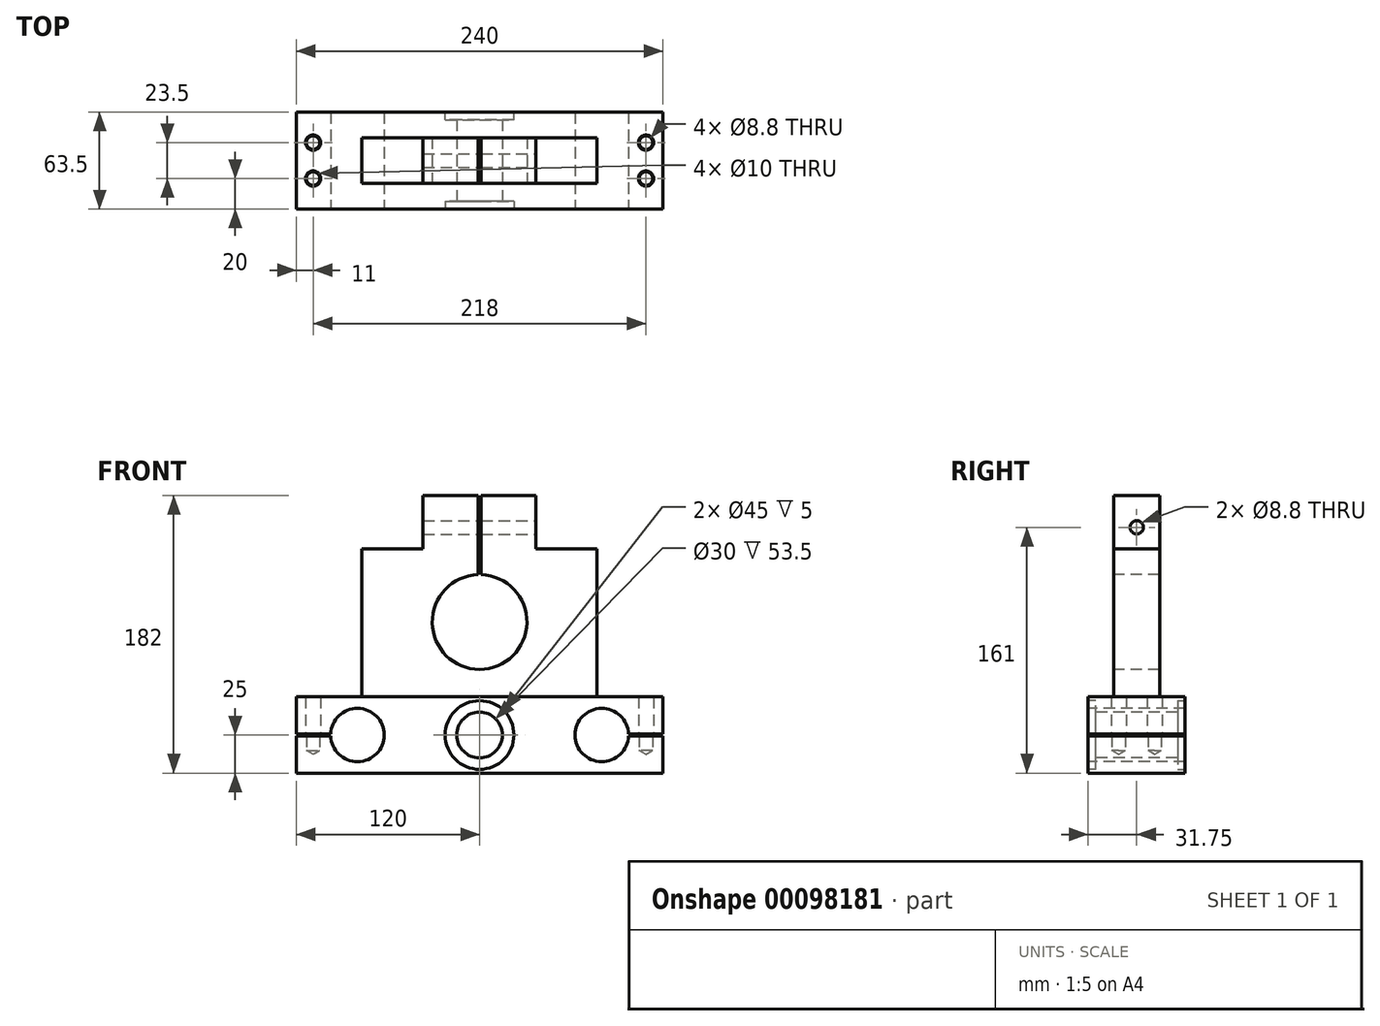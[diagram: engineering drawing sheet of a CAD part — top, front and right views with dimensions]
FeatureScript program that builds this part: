
annotation { "Feature Type Name" : "Feature", "Feature Type Description" : "" }
export const myFeature = defineFeature(function(context is Context, id is Id, definition is map)
    precondition{}
    {
        {
            var Q0;
            Q0=qCreatedBy(makeId("Front.planeOp"),FACE);
            var sketch = newSketch(context, id + "F0", { "sketchPlane" : qUnion([Q0])});
            skLineSegment(sketch, "E0.bottom", {"start": v(0, 0) * mm, "end": v(240, 0) * mm});
            skLineSegment(sketch, "E0.top", {"start": v(0, 50) * mm, "end": v(240, 50) * mm});
            skLineSegment(sketch, "E0.left", {"start": v(0, 0) * mm, "end": v(0, 50) * mm});
            skLineSegment(sketch, "E0.right", {"start": v(240, 0) * mm, "end": v(240, 50) * mm});
            skSolve(sketch);
        }
        {
            var Q0;
            Q0=makeQuery(id+"F0.imprint","IMPRINT",FACE,{"disambiguationData":[TD([[makeQuery(id+"F0.imprint","IMPRINT",EDGE,{"derivedFrom":sQuery(id+"F0.wireOp",EDGE,"E0.bottom")}),1.0]])]});
            extrude(context, id + "F1", {"entities" : qUnion([Q0]), "depth" : 63.5 * mm});
        }
        {
            var Q0;
            Q0=makeQuery(id+"F1.opExtrude","CAP_FACE",FACE,{"disambiguationData":[OSD([sQuery(id+"F0.wireOp",EDGE,"E0.bottom"),sQuery(id+"F0.wireOp",EDGE,"E0.top"),sQuery(id+"F0.wireOp",EDGE,"E0.left"),sQuery(id+"F0.wireOp",EDGE,"E0.right")])],"isStart":false});
            var sketch = newSketch(context, id + "F2", { "sketchPlane" : qUnion([Q0])});
            skLineSegment(sketch, "E1", {"start": v(0, 25) * mm, "end": v(240, 25) * mm});
            skLineSegment(sketch, "E2", {"start": v(120, 50) * mm, "end": v(120, 0) * mm});
            skLineSegment(sketch, "E3", {"start": v(120, 25) * mm, "end": v(200, 25) * mm});
            skLineSegment(sketch, "E4", {"start": v(120, 25) * mm, "end": v(40, 25) * mm});
            skCircle(sketch, "E5", {"center": v(40, 25) * mm, "radius": 17.5 * mm});
            skCircle(sketch, "E6", {"center": v(200, 25) * mm, "radius": 17.5 * mm});
            skCircle(sketch, "E7", {"center": v(120, 25) * mm, "radius": 15 * mm});
            skSolve(sketch);
        }
        {
            var Q0;
            Q0 = qSketchRegion(id + "F2", true);
            extrude(context, id + "F3", {"entities" : qUnion([Q0]), "operationType" : NewBodyOperationType.REMOVE, "endBound" : BoundingType.THROUGH_ALL, "oppositeDirection" : true, "depth" : 25 * mm});
        }
        {
            var Q0;
            Q0=makeQuery(id+"F1.opExtrude","CAP_FACE",FACE,{"disambiguationData":[OSD([sQuery(id+"F0.wireOp",EDGE,"E0.bottom"),sQuery(id+"F0.wireOp",EDGE,"E0.top"),sQuery(id+"F0.wireOp",EDGE,"E0.left"),sQuery(id+"F0.wireOp",EDGE,"E0.right")])],"isStart":false});
            var sketch = newSketch(context, id + "F4", { "sketchPlane" : qUnion([Q0])});
            skCircle(sketch, "E8", {"center": v(120, 25) * mm, "radius": 22.5 * mm});
            skSolve(sketch);
        }
        {
            var Q0;
            Q0 = qSketchRegion(id + "F4", true);
            extrude(context, id + "F5", {"entities" : qUnion([Q0]), "operationType" : NewBodyOperationType.REMOVE, "oppositeDirection" : true, "depth" : 5 * mm});
        }
        {
            var Q0;
            Q0=makeQuery(id+"F1.opExtrude","CAP_FACE",FACE,{"disambiguationData":[OSD([sQuery(id+"F0.wireOp",EDGE,"E0.bottom"),sQuery(id+"F0.wireOp",EDGE,"E0.top"),sQuery(id+"F0.wireOp",EDGE,"E0.left"),sQuery(id+"F0.wireOp",EDGE,"E0.right")])],"isStart":true});
            var sketch = newSketch(context, id + "F6", { "sketchPlane" : qUnion([Q0])});
            skCircle(sketch, "E9", {"center": v(-120, 25) * mm, "radius": 22.5 * mm});
            skSolve(sketch);
        }
        {
            var Q0;
            Q0 = qSketchRegion(id + "F6", true);
            extrude(context, id + "F7", {"entities" : qUnion([Q0]), "operationType" : NewBodyOperationType.REMOVE, "oppositeDirection" : true, "depth" : 5 * mm});
        }
        {
            var Q0;
            Q0=makeQuery(id+"F1.opExtrude","CAP_FACE",FACE,{"disambiguationData":[OSD([sQuery(id+"F0.wireOp",EDGE,"E0.bottom"),sQuery(id+"F0.wireOp",EDGE,"E0.top"),sQuery(id+"F0.wireOp",EDGE,"E0.left"),sQuery(id+"F0.wireOp",EDGE,"E0.right")])],"isStart":false});
            var sketch = newSketch(context, id + "F8", { "sketchPlane" : qUnion([Q0])});
            skLineSegment(sketch, "E10", {"start": v(0, 25) * mm, "end": v(33.46, 25) * mm});
            skPoint(sketch, "E10.endSnap0", {"position": v(240, 25) * mm});
            skLineSegment(sketch, "E11.0", {"start": v(0, 24.5) * mm, "end": v(33.46, 24.5) * mm});
            skLineSegment(sketch, "E12.0", {"start": v(0, 25.5) * mm, "end": v(33.46, 25.5) * mm});
            skLineSegment(sketch, "E13", {"start": v(33.46, 25.5) * mm, "end": v(33.46, 24.5) * mm});
            skLineSegment(sketch, "E14", {"start": v(0, 24.5) * mm, "end": v(0, 25.5) * mm});
            skLineSegment(sketch, "E15", {"start": v(240, 25) * mm, "end": v(208.06, 25) * mm});
            skLineSegment(sketch, "E16.0", {"start": v(240, 25.5) * mm, "end": v(208.06, 25.5) * mm});
            skLineSegment(sketch, "E17.0", {"start": v(240, 24.5) * mm, "end": v(208.06, 24.5) * mm});
            skLineSegment(sketch, "E18", {"start": v(208.06, 25.5) * mm, "end": v(208.06, 24.5) * mm});
            skLineSegment(sketch, "E19", {"start": v(240, 24.5) * mm, "end": v(240, 25.5) * mm});
            skSolve(sketch);
        }
        {
            var Q0;
            Q0 = qSketchRegion(id + "F8", true);
            extrude(context, id + "F9", {"entities" : qUnion([Q0]), "operationType" : NewBodyOperationType.REMOVE, "endBound" : BoundingType.THROUGH_ALL, "oppositeDirection" : true, "depth" : 25 * mm});
        }
        {
            var Q0;
            Q0=makeQuery(id+"F1.opExtrude","SWEPT_FACE",FACE,{"disambiguationData":[OSD([sQuery(id+"F0.wireOp",EDGE,"E0.top")])]});
            var sketch = newSketch(context, id + "F10", { "sketchPlane" : qUnion([Q0])});
            skLineSegment(sketch, "E20.0", {"start": v(11, -63.5) * mm, "end": v(11, 0) * mm});
            skLineSegment(sketch, "E21.0", {"start": v(229, -63.5) * mm, "end": v(229, 0) * mm});
            skLineSegment(sketch, "E22.0", {"start": v(0, -20) * mm, "end": v(240, -20) * mm});
            skLineSegment(sketch, "E23.0", {"start": v(0, -43.5) * mm, "end": v(240, -43.5) * mm});
            skPoint(sketch, "E24", {"position": v(11, -20) * mm});
            skPoint(sketch, "E25", {"position": v(11, -43.5) * mm});
            skPoint(sketch, "E26", {"position": v(229, -43.5) * mm});
            skPoint(sketch, "E27", {"position": v(229, -20) * mm});
            skSolve(sketch);
        }
        {
            var Q0;
            Q0=sQuery(id+"F10.wireOp",VERTEX,"E24");
            var Q1;
            Q1=sQuery(id+"F10.wireOp",VERTEX,"E25");
            var Q2;
            Q2=sQuery(id+"F10.wireOp",VERTEX,"E27");
            var Q3;
            Q3=sQuery(id+"F10.wireOp",VERTEX,"E26");
            var Q4;
            Q4=makeQuery(id+"F1.opExtrude","SWEPT_BODY",BODY,{"disambiguationData":[OSD([sQuery(id+"F0.wireOp",EDGE,"E0.bottom"),sQuery(id+"F0.wireOp",EDGE,"E0.top"),sQuery(id+"F0.wireOp",EDGE,"E0.left"),sQuery(id+"F0.wireOp",EDGE,"E0.right")])]});
            hole(context, id + "F11", {"style" : HoleStyle.C_BORE, "endStyle" : HoleEndStyle.BLIND, "holeDiameter" : 8.8 * mm, "cBoreDiameter" : 10 * mm, "cBoreDepth" : 25 * mm, "holeDepth" : 35 * mm, "locations" : qUnion([Q0, Q1, Q2, Q3]), "scope" : qUnion([Q4]), "startStyle" : HoleStartStyle.PART});
        }
        {
            var Q0;
            Q0=makeQuery(id+"F1.opExtrude","SWEPT_FACE",FACE,{"disambiguationData":[OSD([sQuery(id+"F0.wireOp",EDGE,"E0.top")])]});
            var sketch = newSketch(context, id + "F12", { "sketchPlane" : qUnion([Q0])});
            skLineSegment(sketch, "E28.0", {"start": v(43, -63.5) * mm, "end": v(43, 0) * mm});
            skLineSegment(sketch, "E29.0", {"start": v(197, -63.5) * mm, "end": v(197, 0) * mm});
            skLineSegment(sketch, "E30.0", {"start": v(0, -16.75) * mm, "end": v(240, -16.75) * mm});
            skLineSegment(sketch, "E31.0", {"start": v(0, -46.75) * mm, "end": v(240, -46.75) * mm});
            skSolve(sketch);
        }
        {
            var Q0;
            {var subQ0=sQuery(id+"F12.wireOp",EDGE,"E31.0");var subQ1=sQuery(id+"F12.wireOp",EDGE,"E28.0");var subQ2=makeQuery(id+"F12.imprint","INTERSECT",VERTEX,{"derivedFrom":[subQ1,subQ0]});Q0=makeQuery(id+"F12.imprint","IMPRINT",FACE,{"disambiguationData":[TD([[makeQuery(id+"F12.imprint","IMPRINT",EDGE,{"disambiguationData":[TD([[subQ2,-1.0]])],"derivedFrom":subQ1}),-1.0]])]});}
            extrude(context, id + "F13", {"entities" : qUnion([Q0]), "operationType" : NewBodyOperationType.ADD, "depth" : 132 * mm});
        }
        {
            var Q0;
            Q0=makeQuery(id+"F1.opExtrude","CAP_FACE",FACE,{"disambiguationData":[OSD([sQuery(id+"F0.wireOp",EDGE,"E0.bottom"),sQuery(id+"F0.wireOp",EDGE,"E0.top"),sQuery(id+"F0.wireOp",EDGE,"E0.left"),sQuery(id+"F0.wireOp",EDGE,"E0.right")])],"isStart":false});
            var sketch = newSketch(context, id + "F14", { "sketchPlane" : qUnion([Q0])});
            skLineSegment(sketch, "E32", {"start": v(120, 25) * mm, "end": v(120, 99) * mm});
            skCircle(sketch, "E33", {"center": v(120, 99) * mm, "radius": 31 * mm});
            skSolve(sketch);
        }
        {
            var Q0;
            Q0 = qSketchRegion(id + "F14", true);
            var Q1;
            Q1=makeQuery(id+"F14.imprint","IMPRINT",FACE,{"disambiguationData":[TD([[makeQuery(id+"F14.imprint","IMPRINT",EDGE,{"derivedFrom":sQuery(id+"F14.wireOp",EDGE,"E33")}),1.0]])]});
            extrude(context, id + "F15", {"entities" : qUnion([Q0, Q1]), "operationType" : NewBodyOperationType.REMOVE, "endBound" : BoundingType.THROUGH_ALL, "oppositeDirection" : true, "depth" : 25 * mm});
        }
        {
            var Q0;
            Q0=makeQuery(id+"F13.opExtrude","SWEPT_FACE",FACE,{"disambiguationData":[OSD([sQuery(id+"F12.wireOp",EDGE,"E31.0")])]});
            var sketch = newSketch(context, id + "F16", { "sketchPlane" : qUnion([Q0])});
            skLineSegment(sketch, "E34", {"start": v(120, 99) * mm, "end": v(120, 203.97) * mm});
            skLineSegment(sketch, "E35.0", {"start": v(121, 99) * mm, "end": v(121, 203.97) * mm});
            skLineSegment(sketch, "E36.0", {"start": v(119, 99) * mm, "end": v(119, 203.97) * mm});
            skLineSegment(sketch, "E37", {"start": v(121, 203.97) * mm, "end": v(119, 203.97) * mm});
            skLineSegment(sketch, "E38", {"start": v(121, 99) * mm, "end": v(119, 99) * mm});
            skSolve(sketch);
        }
        {
            var Q0;
            Q0 = qSketchRegion(id + "F16", true);
            extrude(context, id + "F17", {"entities" : qUnion([Q0]), "operationType" : NewBodyOperationType.REMOVE, "endBound" : BoundingType.THROUGH_ALL, "oppositeDirection" : true, "depth" : 25 * mm});
        }
        {
            var Q0;
            Q0=makeQuery(id+"F13.opExtrude","SWEPT_FACE",FACE,{"disambiguationData":[OSD([sQuery(id+"F12.wireOp",EDGE,"E31.0")])]});
            var sketch = newSketch(context, id + "F18", { "sketchPlane" : qUnion([Q0])});
            skLineSegment(sketch, "E39.bottom", {"start": v(83, 147) * mm, "end": v(43, 147) * mm});
            skLineSegment(sketch, "E39.top", {"start": v(83, 182) * mm, "end": v(43, 182) * mm});
            skLineSegment(sketch, "E39.left", {"start": v(83, 147) * mm, "end": v(83, 182) * mm});
            skLineSegment(sketch, "E39.right", {"start": v(43, 147) * mm, "end": v(43, 182) * mm});
            skPoint(sketch, "E40.oppositeSnap0", {"position": v(63, 147) * mm});
            skLineSegment(sketch, "E40.bottom", {"start": v(197, 182) * mm, "end": v(157, 182) * mm});
            skLineSegment(sketch, "E40.top", {"start": v(197, 147) * mm, "end": v(157, 147) * mm});
            skLineSegment(sketch, "E40.left", {"start": v(197, 182) * mm, "end": v(197, 147) * mm});
            skLineSegment(sketch, "E40.right", {"start": v(157, 182) * mm, "end": v(157, 147) * mm});
            skSolve(sketch);
        }
        {
            var Q0;
            Q0 = qSketchRegion(id + "F18", true);
            extrude(context, id + "F19", {"entities" : qUnion([Q0]), "operationType" : NewBodyOperationType.REMOVE, "endBound" : BoundingType.THROUGH_ALL, "oppositeDirection" : true, "depth" : 25 * mm});
        }
        {
            var Q0;
            Q0=makeQuery(id+"F19.boolean.opBoolean","COPY",FACE,{"derivedFrom":makeQuery(id+"F19.opExtrude","SWEPT_FACE",FACE,{"disambiguationData":[OSD([sQuery(id+"F18.wireOp",EDGE,"E39.left")])]})});
            var sketch = newSketch(context, id + "F20", { "sketchPlane" : qUnion([Q0])});
            skLineSegment(sketch, "E41", {"start": v(16.75, 182) * mm, "end": v(16.75, 156) * mm});
            skLineSegment(sketch, "E42", {"start": v(16.75, 156) * mm, "end": v(46.75, 156) * mm});
            skLineSegment(sketch, "E43", {"start": v(31.75, 182) * mm, "end": v(31.75, 156) * mm});
            skPoint(sketch, "E44", {"position": v(31.75, 156) * mm});
            skLineSegment(sketch, "E45.0", {"start": v(16.75, 161) * mm, "end": v(46.75, 161) * mm});
            skPoint(sketch, "E46", {"position": v(31.75, 161) * mm});
            skSolve(sketch);
        }
        {
            var Q0;
            Q0=sQuery(id+"F20.wireOp",VERTEX,"E46");
            var Q1;
            Q1=makeQuery(id+"F1.opExtrude","SWEPT_BODY",BODY,{"disambiguationData":[OSD([sQuery(id+"F0.wireOp",EDGE,"E0.bottom"),sQuery(id+"F0.wireOp",EDGE,"E0.top"),sQuery(id+"F0.wireOp",EDGE,"E0.left"),sQuery(id+"F0.wireOp",EDGE,"E0.right")])]});
            hole(context, id + "F21", {"style" : HoleStyle.SIMPLE, "endStyle" : HoleEndStyle.BLIND, "standardTappedOrClearance" : lookupTablePath({ "standard" : "ISO", "fit" : "Normal", "size" : "M8", "type" : "Clearance" }), "standardBlindInLast" : lookupTablePath({ "fit" : "Standard", "standard" : "ISO", "size" : "M8", "type" : "Clearance" }), "holeDiameter" : 8.8 * mm, "holeDepth" : 93 * mm, "locations" : qUnion([Q0]), "scope" : qUnion([Q1]), "startStyle" : HoleStartStyle.PART});
        }
    });
